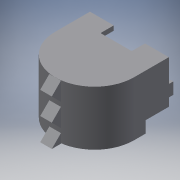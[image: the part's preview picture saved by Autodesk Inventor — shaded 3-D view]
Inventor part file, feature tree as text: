
AUTODESK INVENTOR PART (.ipt)
format: ipt  version: 2016 (Build 200138000, 138)  size: 260,608 bytes
history: native  units: in
note: dims shown in document units (in); Inventor stores cm internally (conversion verified against a paired STEP export)
features: sketch x12, extrude x11, reference x10, projected_geometry x2, plane x1, fillet x1
ambient origin geometry x8: Origin, YZ Plane, XZ Plane, XY Plane, X Axis, Y Axis, Z Axis, Center Point
bodies: Solid1 (feature_tree)
feature tree (37):
  extrude  "Extrusion1"  Depth=1.5in TaperAngle=0.0deg
  extrude  "Extrusion2"  Depth=0.1969in TaperAngle=0.0deg
  extrude  "Extrusion3"  Depth=0.7874in
  plane  "Work Plane1"
  sketch  "Sketch5"  dims[d11=0.3937in d12=1.9685in d14=0.9774in d15=0.3937in d17=1.0in]
  extrude  "Extrusion5"  Depth=0.3937in
  extrude  "Extrusion6"  Depth=0.197in TaperAngle=0.0deg
  extrude  "Extrusion7"  Depth=2.0in TaperAngle=0.0deg
  extrude  "Extrusion8"  Depth=0.5in
  extrude  "Extrusion9"  Depth=0.5in TaperAngle=0.0deg
  extrude  "Extrusion10"  Depth=0.1969in
  extrude  "Extrusion11"  Depth=1.0in TaperAngle=0.0deg
  extrude  "Extrusion12"  [1 undecoded]
  fillet  "Fillet1"  [1 undecoded]
  sketch  "Sketch1"  dims[d0=0.1969in d1=1.5in d2=0.0in]
  reference  "Reference1"
  sketch  "Sketch2"  dims[d3=4.6969in d4=0.0in d5=0.1969in d6=0.0in]
  sketch  "Sketch3"  dims[d9=-1.697in d10=0.7874in]
  sketch  "Sketch6"  dims[d19=0.5in d20=0.0in d21=0.197in d22=0.0in]
  sketch  "Sketch8"  dims[d23=2.0in d24=0.0in d25=2.0in d26=0.0in]
  reference  "Reference3"
  reference  "Reference5"
  reference  "Reference6"
  reference  "Reference7"
  reference  "Reference8"
  sketch  "Sketch9"  dims[d27=16.0in d28=0.0in d29=0.5in]
  reference  "Reference10"
  sketch  "Sketch10"  dims[d30=435.0in d31=0.0in d32=0.5in d33=0.0in]
  reference  "Reference11"
  sketch  "Sketch11"  dims[d34=0.0787in d35=0.1969in]
  sketch  "Sketch12"  dims[d36=0.1969in d37=1.0in d38=0.0in]
  sketch  "Sketch13"  dims[d39=0.0394in]
  projected_geometry  "Projected Loop1"
  projected_geometry  "Projected Loop2"
  sketch  "Sketch14"
  reference  "Reference12"
  reference  "Reference13"
note: 2 required parameter values undecoded (feature->parameter linkage not recoverable at this tier; creation-order binding heuristic only, values carry confidence <= 0.55)
